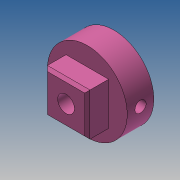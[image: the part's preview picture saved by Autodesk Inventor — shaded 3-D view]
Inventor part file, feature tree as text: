
AUTODESK INVENTOR PART (.ipt)
format: ipt  version: 2017 (Build 210142000, 142)  size: 195,072 bytes
history: native  units: mm
features: extrude x4, sketch x3, chamfer x2, other x1, projected_geometry x1
ambient origin geometry x8: Origin, YZ Plane, XZ Plane, XY Plane, X Axis, Y Axis, Z Axis, Center Point
bodies: Body1 (feature_tree)
feature tree (11):
  other  "Sólido1"
  extrude  "Extrusión1"  Depth=11.85mm
  sketch  "Boceto2"  dims[d3=6.650287mm d4=3.7mm]
  extrude  "Extrusión2"  Depth=3.7mm
  extrude  "Extrusión3"  Depth=16.0mm
  extrude  "Extrusión4"  TaperAngle=120.0deg  [1 undecoded]
  chamfer  "Chaflán1"  Distance=3.9mm
  chamfer  "Chaflán3"  Distance=16.0mm
  sketch  "Boceto1"  dims[d0=6.3mm d2=11.85mm]
  projected_geometry  "Contorno proyectado1"
  sketch  "Boceto3"  dims[d5=10.0mm d6=0.0mm d7=4.2mm d8=120.0deg d9=3.9mm d10=16.0mm d11=0.0mm d12=4.0mm d13=0.0mm d14=8.0mm d15=0.0mm d16=30.0mm d18=360.0deg d23=1.0mm d24=2.0mm d25=45.0deg d26=30.0mm d27=4.075mm d28=4.075mm d32=16.0mm d33=55.0mm d36=1.0mm d37=2.0mm d38=45.0deg]
note: 1 required parameter value undecoded (feature->parameter linkage not recoverable at this tier; creation-order binding heuristic only, values carry confidence <= 0.55)
